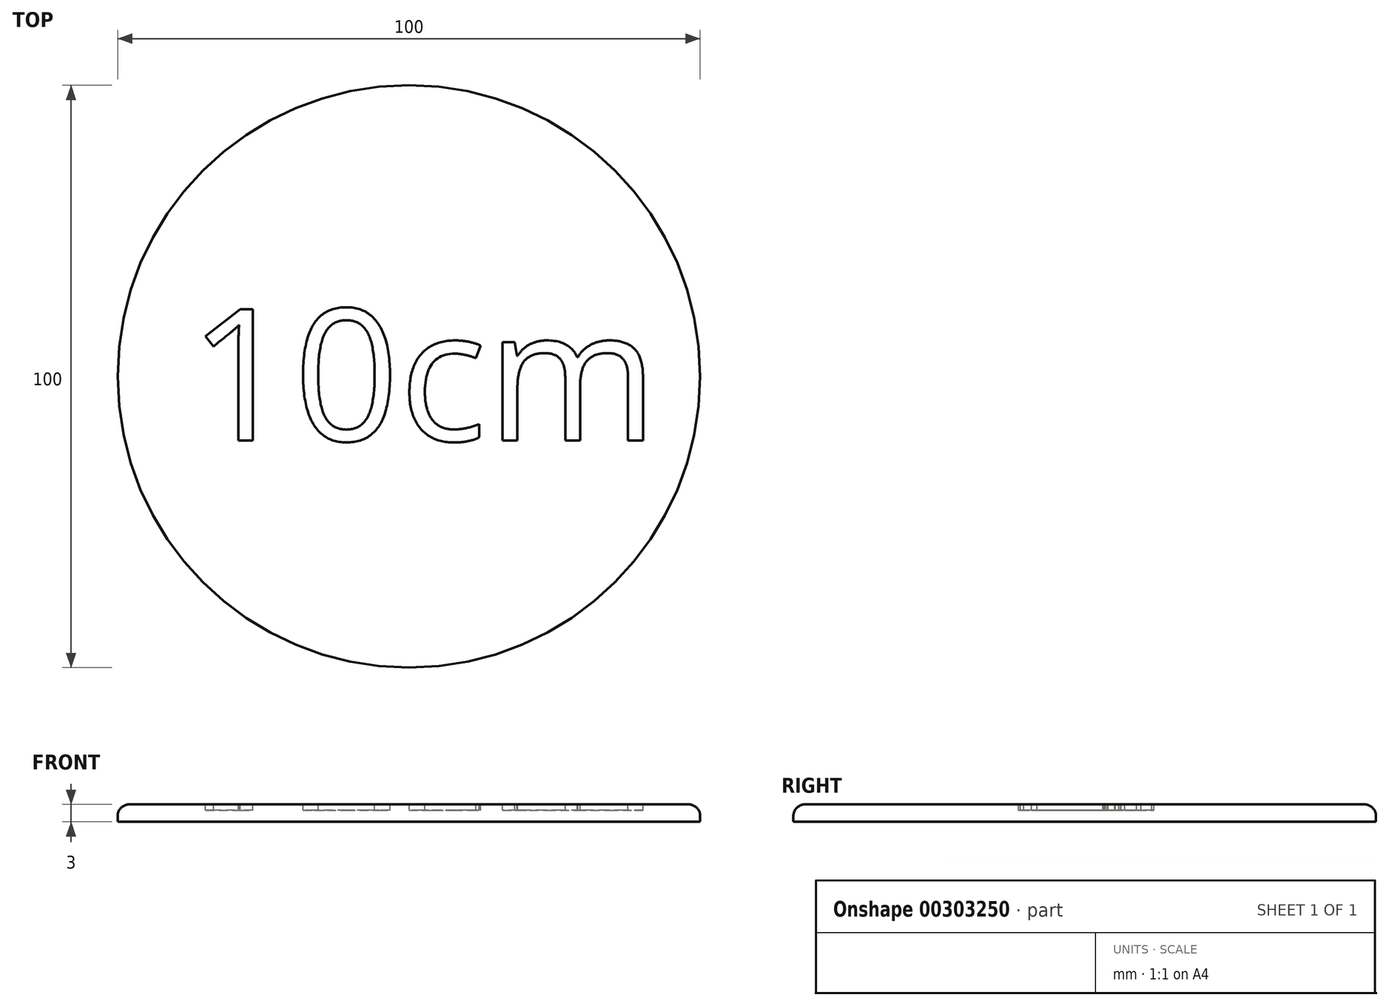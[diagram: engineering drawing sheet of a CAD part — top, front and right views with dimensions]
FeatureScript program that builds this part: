
annotation { "Feature Type Name" : "Feature", "Feature Type Description" : "" }
export const myFeature = defineFeature(function(context is Context, id is Id, definition is map)
    precondition{}
    {
        {
            var Q0;
            Q0=qCreatedBy(makeId("Right.planeOp"),FACE);
            var sketch = newSketch(context, id + "F0", { "sketchPlane" : qUnion([Q0])});
            skLineSegment(sketch, "E0.bottom", {"start": v(0, 0) * mm, "end": v(-50, 0) * mm});
            skLineSegment(sketch, "E0.top", {"start": v(0, 3) * mm, "end": v(-50, 3) * mm});
            skLineSegment(sketch, "E0.left", {"start": v(0, 0) * mm, "end": v(0, 3) * mm});
            skLineSegment(sketch, "E0.right", {"start": v(-50, 0) * mm, "end": v(-50, 3) * mm});
            skLineSegment(sketch, "E1", {"start": v(0, 0) * mm, "end": v(0, 3.09) * mm, "construction": true});
            skSolve(sketch);
        }
        {
            var Q0;
            Q0 = qSketchRegion(id + "F0", true);
            var Q1;
            Q1=sQuery(id+"F0.wireOp",EDGE,"E1");
            revolve(context, id + "F1", {"entities" : qUnion([Q0]), "axis" : qUnion([Q1]), "revolveType" : RevolveType.FULL});
        }
        {
            var Q0;
            Q0=makeQuery(id+"F1.opRevolve","SWEPT_EDGE",EDGE,{"disambiguationData":[OSD([sQuery(id+"F0.wireOp",EDGE,"E0.top"),sQuery(id+"F0.wireOp",EDGE,"E0.right")])]});
            fillet(context, id + "F2", {"entities" : qUnion([Q0]), "radius" : 2 * mm, "tangentPropagation" : true, "allowEdgeOverflow" : false});
        }
        {
            var Q0;
            Q0=makeQuery(id+"F1.opRevolve","SWEPT_FACE",FACE,{"disambiguationData":[OSD([sQuery(id+"F0.wireOp",EDGE,"E0.top")])]});
            var sketch = newSketch(context, id + "F3", { "sketchPlane" : qUnion([Q0])});
            skText(sketch, "E2", { "text": "10cm\n", "fontName": "OpenSans-Regular.ttf"});
            const initialGuessF3  = {"E2": [-0.0378, -0.01103, 1, 0, 0.02274]};
            skSetInitialGuess(sketch, initialGuessF3);
            skSolve(sketch);
        }
        {
            var Q0;
            Q0 = qSketchRegion(id + "F3", true);
            extrude(context, id + "F4", {"entities" : qUnion([Q0]), "operationType" : NewBodyOperationType.REMOVE, "oppositeDirection" : true, "depth" : 1 * mm});
        }
    });
